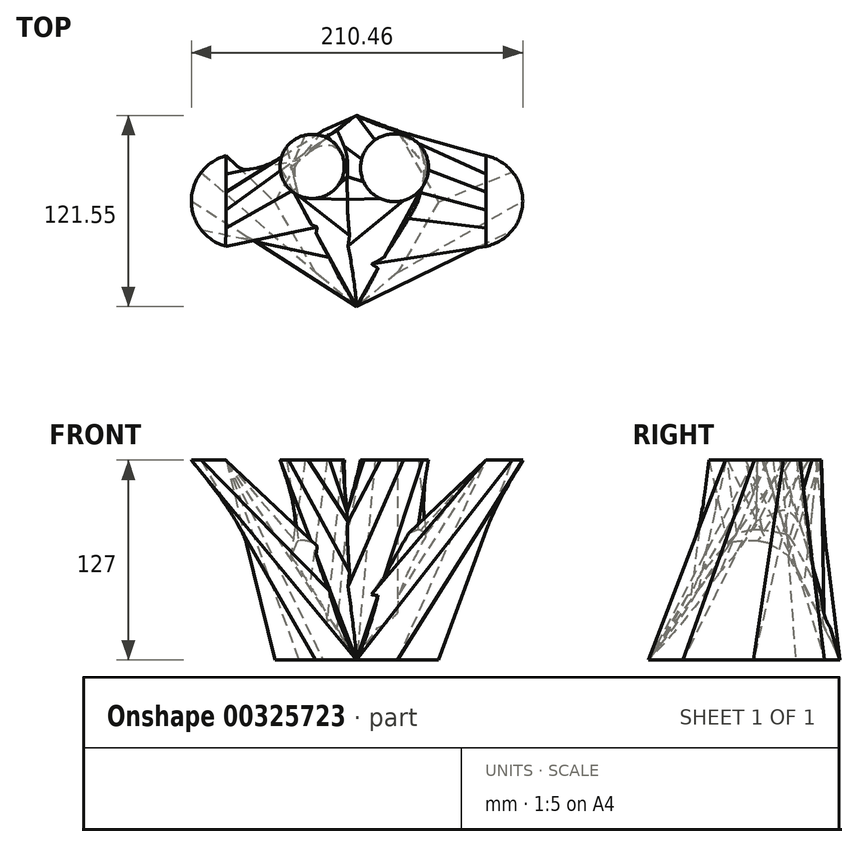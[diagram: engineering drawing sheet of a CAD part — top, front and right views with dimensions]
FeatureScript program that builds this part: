
annotation { "Feature Type Name" : "Feature", "Feature Type Description" : "" }
export const myFeature = defineFeature(function(context is Context, id is Id, definition is map)
    precondition{}
    {
        {
            var Q0;
            Q0=qCreatedBy(makeId("Top.planeOp"),FACE);
            var sketch = newSketch(context, id + "F0", { "sketchPlane" : qUnion([Q0])});
            skCircle(sketch, "E0.cCircle", {"center": v(0, 0) * mm, "radius": 45 * mm, "construction": true});
            skLineSegment(sketch, "E0.0", {"start": v(25.99, 45) * mm, "end": v(51.97, 0) * mm});
            skLineSegment(sketch, "E0.1", {"start": v(51.97, 0) * mm, "end": v(25.99, -45) * mm});
            skLineSegment(sketch, "E0.3", {"start": v(-25.99, -45) * mm, "end": v(-51.97, 0) * mm});
            skLineSegment(sketch, "E0.4", {"start": v(-51.97, 0) * mm, "end": v(-36.6, 26.61) * mm});
            skPoint(sketch, "E0.0.midPoint", {"position": v(38.98, 22.5) * mm});
            skLineSegment(sketch, "E1", {"start": v(25.99, 45) * mm, "end": v(0, 54.94) * mm});
            skLineSegment(sketch, "E2", {"start": v(-35.87, 27.18) * mm, "end": v(-36.6, 26.61) * mm});
            skLineSegment(sketch, "E3", {"start": v(25.99, -45) * mm, "end": v(0, -66.61) * mm});
            skLineSegment(sketch, "E4", {"start": v(0, -66.61) * mm, "end": v(-25.99, -45) * mm});
            skLineSegment(sketch, "E5", {"start": v(0, 54.94) * mm, "end": v(-21.22, 45.2) * mm});
            skLineSegment(sketch, "E6", {"start": v(-21.22, 45.2) * mm, "end": v(-36.6, 26.61) * mm});
            skSolve(sketch);
        }
        {
            var Q0;
            Q0=qCreatedBy(makeId("Top.planeOp"),FACE);
            cPlane(context, id + "F1", {"entities" : qUnion([Q0]), "cplaneType" : CPlaneType.OFFSET, "offset" : 127 * mm, "width" : 152.4 * mm, "height" : 152.4 * mm});
        }
        {
            var Q0;
            Q0=qCreatedBy(id+"F1.planeOp",FACE);
            var sketch = newSketch(context, id + "F2", { "sketchPlane" : qUnion([Q0])});
            skCircle(sketch, "E7", {"center": v(-28.23, 22.5) * mm, "radius": 20.36 * mm});
            skCircle(sketch, "E8", {"center": v(24.04, 21.64) * mm, "radius": 21.53 * mm});
            skLineSegment(sketch, "E9.bottom", {"start": v(23.63, -12.23) * mm, "end": v(-33.6, -12.23) * mm});
            skLineSegment(sketch, "E9.top", {"start": v(23.63, -29.46) * mm, "end": v(-33.6, -29.46) * mm});
            skLineSegment(sketch, "E9.left", {"start": v(23.63, -12.23) * mm, "end": v(23.63, -29.46) * mm});
            skLineSegment(sketch, "E9.right", {"start": v(-33.6, -12.23) * mm, "end": v(-33.6, -29.46) * mm});
            skPoint(sketch, "E9.middle", {"position": v(-4.99, -20.84) * mm});
            skArc(sketch, "E10", {"start": v(-82.83, 29.31) * mm, "mid": v(-104.99, 0.66) * mm, "end": v(-83.14, -28.22) * mm});
            skLineSegment(sketch, "E11", {"start": v(-83.14, -28.22) * mm, "end": v(-82.83, 29.31) * mm});
            skLineSegment(sketch, "E12", {"start": v(82.09, 29.31) * mm, "end": v(82.09, -28.22) * mm});
            skArc(sketch, "E13", {"start": v(82.09, -28.22) * mm, "mid": v(105.47, 0.54) * mm, "end": v(82.09, 29.31) * mm});
            skSolve(sketch);
        }
        {
            var Q0;
            Q0=makeQuery(id+"F2.imprint","IMPRINT",FACE,{"disambiguationData":[TD([[makeQuery(id+"F2.imprint","IMPRINT",EDGE,{"derivedFrom":sQuery(id+"F2.wireOp",EDGE,"E7")}),1.0]])]});
            var Q1;
            Q1=makeQuery(id+"F0.imprint","IMPRINT",FACE,{"disambiguationData":[TD([[makeQuery(id+"F0.imprint","IMPRINT",EDGE,{"derivedFrom":sQuery(id+"F0.wireOp",EDGE,"E0.0")}),-1.0]])]});
            loft(context, id + "F3", {"sheetProfilesArray" : [{ "sheetProfileEntities" : qUnion([Q0]) }, { "sheetProfileEntities" : qUnion([Q1]) }]});
        }
        {
            var Q1;
            Q1=makeQuery(id+"F2.imprint","IMPRINT",FACE,{"disambiguationData":[TD([[makeQuery(id+"F2.imprint","IMPRINT",EDGE,{"derivedFrom":sQuery(id+"F2.wireOp",EDGE,"E8")}),1.0]])]});
            var Q2;
            Q2=makeQuery(id+"F0.imprint","IMPRINT",FACE,{"disambiguationData":[TD([[makeQuery(id+"F0.imprint","IMPRINT",EDGE,{"derivedFrom":sQuery(id+"F0.wireOp",EDGE,"E0.0")}),-1.0]])]});
            loft(context, id + "F4", {"operationType" : NewBodyOperationType.ADD, "sheetProfilesArray" : [{ "sheetProfileEntities" : qUnion([Q1]) }, { "sheetProfileEntities" : qUnion([Q2]) }]});
        }
        {
            var Q1;
            Q1=makeQuery(id+"F0.imprint","IMPRINT",FACE,{"disambiguationData":[TD([[makeQuery(id+"F0.imprint","IMPRINT",EDGE,{"derivedFrom":sQuery(id+"F0.wireOp",EDGE,"E0.0")}),-1.0]])]});
            var Q2;
            Q2=makeQuery(id+"F2.imprint","IMPRINT",FACE,{"disambiguationData":[TD([[makeQuery(id+"F2.imprint","IMPRINT",EDGE,{"derivedFrom":sQuery(id+"F2.wireOp",EDGE,"E12")}),1.0]])]});
            loft(context, id + "F5", {"operationType" : NewBodyOperationType.ADD, "sheetProfilesArray" : [{ "sheetProfileEntities" : qUnion([Q1]) }, { "sheetProfileEntities" : qUnion([Q2]) }]});
        }
        {
            var Q1;
            Q1=makeQuery(id+"F2.imprint","IMPRINT",FACE,{"disambiguationData":[TD([[makeQuery(id+"F2.imprint","IMPRINT",EDGE,{"derivedFrom":sQuery(id+"F2.wireOp",EDGE,"E10")}),1.0]])]});
            var Q2;
            Q2=makeQuery(id+"F0.imprint","IMPRINT",FACE,{"disambiguationData":[TD([[makeQuery(id+"F0.imprint","IMPRINT",EDGE,{"derivedFrom":sQuery(id+"F0.wireOp",EDGE,"E0.0")}),-1.0]])]});
            loft(context, id + "F6", {"operationType" : NewBodyOperationType.ADD, "sheetProfilesArray" : [{ "sheetProfileEntities" : qUnion([Q1]) }, { "sheetProfileEntities" : qUnion([Q2]) }]});
        }
    });
